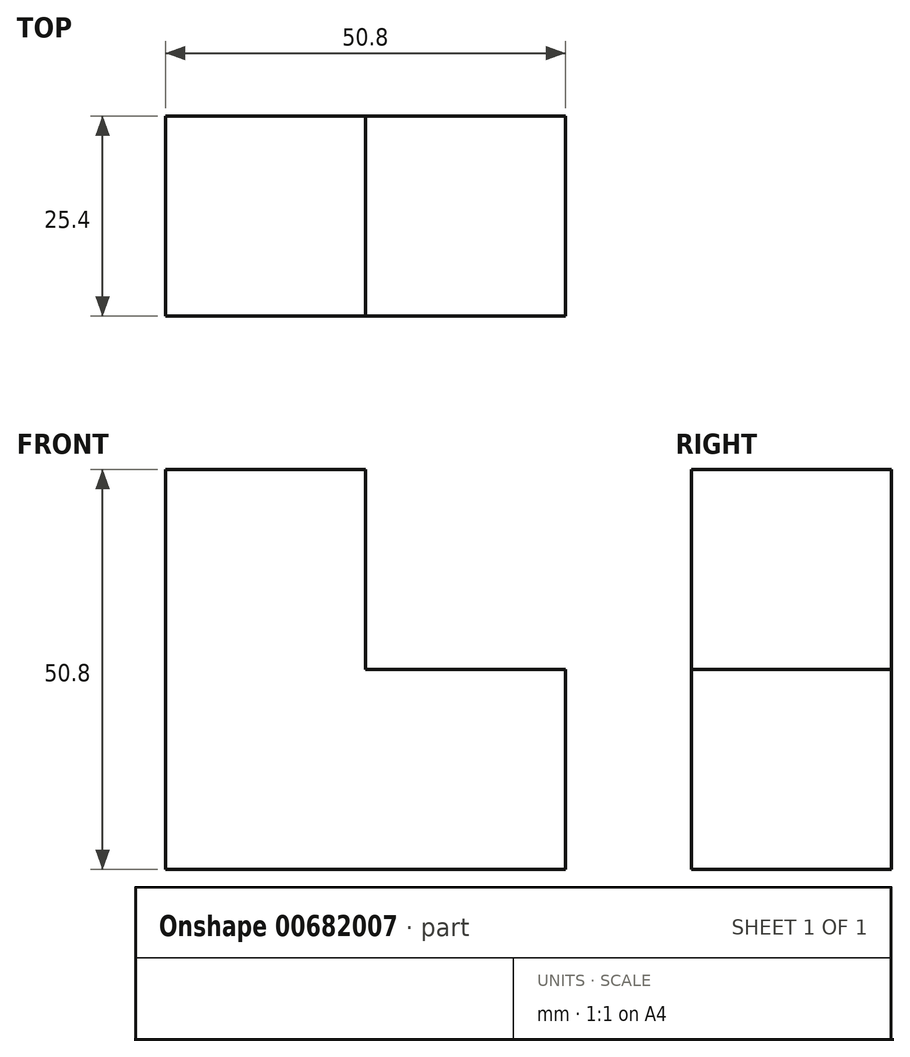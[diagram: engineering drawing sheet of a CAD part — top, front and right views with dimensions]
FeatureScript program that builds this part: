
annotation { "Feature Type Name" : "Feature", "Feature Type Description" : "" }
export const myFeature = defineFeature(function(context is Context, id is Id, definition is map)
    precondition{}
    {
        {
            var Q0;
            Q0=qCreatedBy(makeId("Front.planeOp"),FACE);
            var sketch = newSketch(context, id + "F0", { "sketchPlane" : qUnion([Q0])});
            skLineSegment(sketch, "E0", {"start": v(0, 0) * mm, "end": v(-50.8, 0) * mm});
            skLineSegment(sketch, "E1", {"start": v(-50.8, 0) * mm, "end": v(-50.8, 50.8) * mm});
            skLineSegment(sketch, "E2", {"start": v(-50.8, 50.8) * mm, "end": v(-25.4, 50.8) * mm});
            skLineSegment(sketch, "E3", {"start": v(-25.4, 50.8) * mm, "end": v(-25.4, 25.4) * mm});
            skLineSegment(sketch, "E4", {"start": v(-25.4, 25.4) * mm, "end": v(0, 25.4) * mm});
            skLineSegment(sketch, "E5", {"start": v(0, 25.4) * mm, "end": v(0, 0) * mm});
            skSolve(sketch);
        }
        {
            var Q0;
            Q0=makeQuery(id+"F0.imprint","IMPRINT",FACE,{"disambiguationData":[TD([[makeQuery(id+"F0.imprint","IMPRINT",EDGE,{"derivedFrom":sQuery(id+"F0.wireOp",EDGE,"E0")}),-1.0]])]});
            extrude(context, id + "F1", {"entities" : qUnion([Q0]), "depth" : 25.4 * mm, "offsetDistance" : 25.4 * mm});
        }
    });
